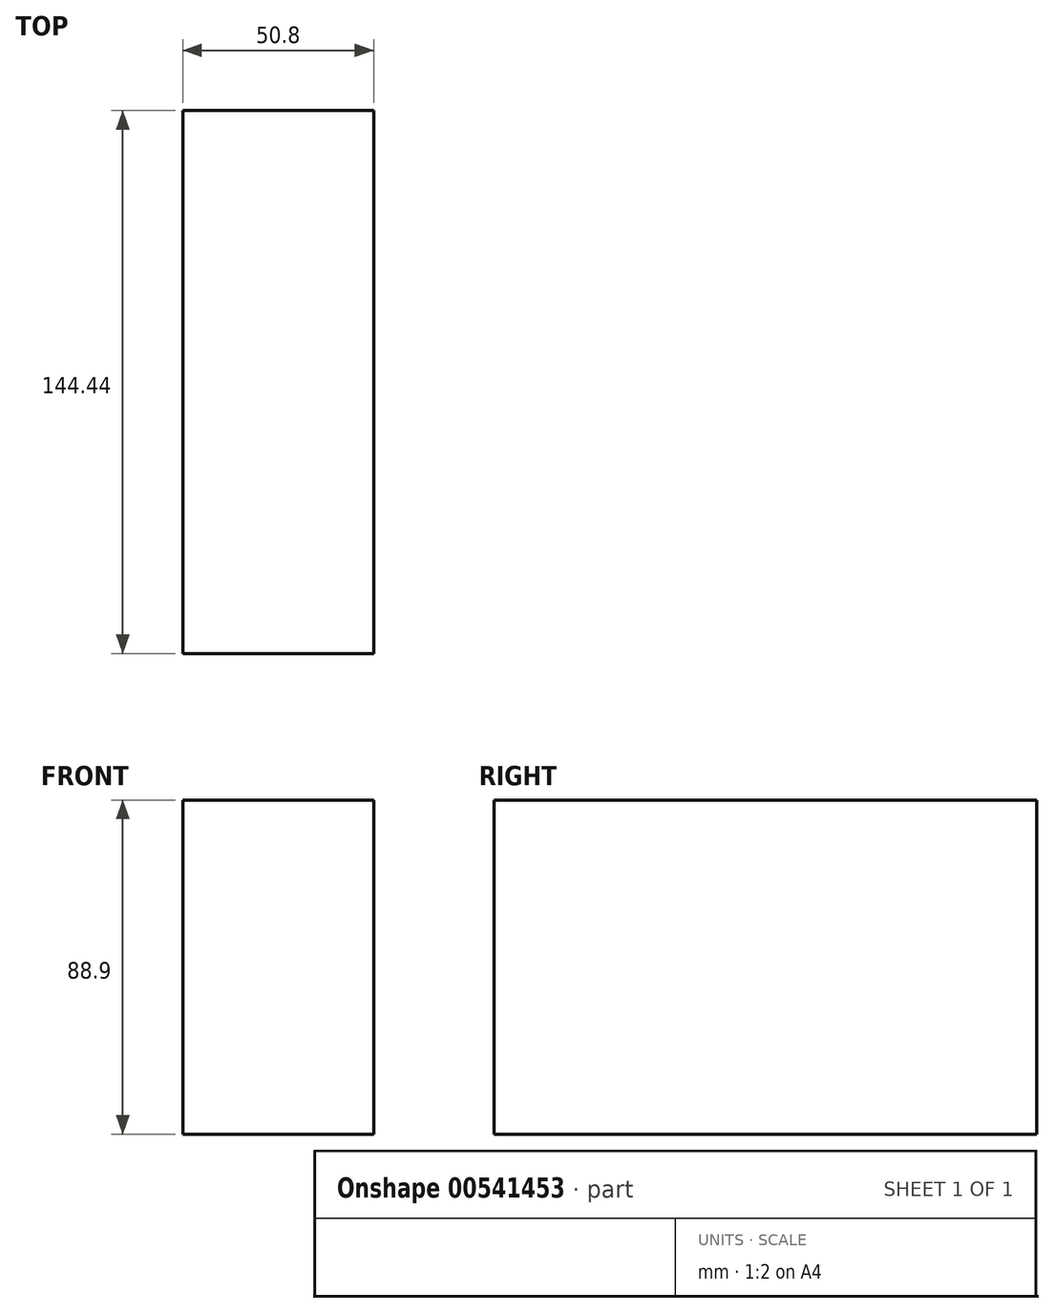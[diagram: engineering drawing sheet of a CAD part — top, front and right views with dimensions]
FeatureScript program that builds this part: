
annotation { "Feature Type Name" : "Feature", "Feature Type Description" : "" }
export const myFeature = defineFeature(function(context is Context, id is Id, definition is map)
    precondition{}
    {
        {
            var Q0;
            Q0=qCreatedBy(makeId("Right.planeOp"),FACE);
            var sketch = newSketch(context, id + "F0", { "sketchPlane" : qUnion([Q0])});
            skLineSegment(sketch, "E0.bottom", {"start": v(-105.3, 76.32) * mm, "end": v(39.14, 76.32) * mm});
            skLineSegment(sketch, "E0.top", {"start": v(-105.3, -12.58) * mm, "end": v(39.14, -12.58) * mm});
            skLineSegment(sketch, "E0.left", {"start": v(-105.3, 76.32) * mm, "end": v(-105.3, -12.58) * mm});
            skLineSegment(sketch, "E0.right", {"start": v(39.14, 76.32) * mm, "end": v(39.14, -12.58) * mm});
            skSolve(sketch);
        }
        {
            var Q0;
            Q0=makeQuery(id+"F0.imprint","IMPRINT",FACE,{"disambiguationData":[TD([[makeQuery(id+"F0.imprint","IMPRINT",EDGE,{"derivedFrom":sQuery(id+"F0.wireOp",EDGE,"E0.bottom")}),-1.0]])]});
            extrude(context, id + "F1", {"entities" : qUnion([Q0]), "depth" : 50.8 * mm, "offsetDistance" : 25.4 * mm});
        }
    });
